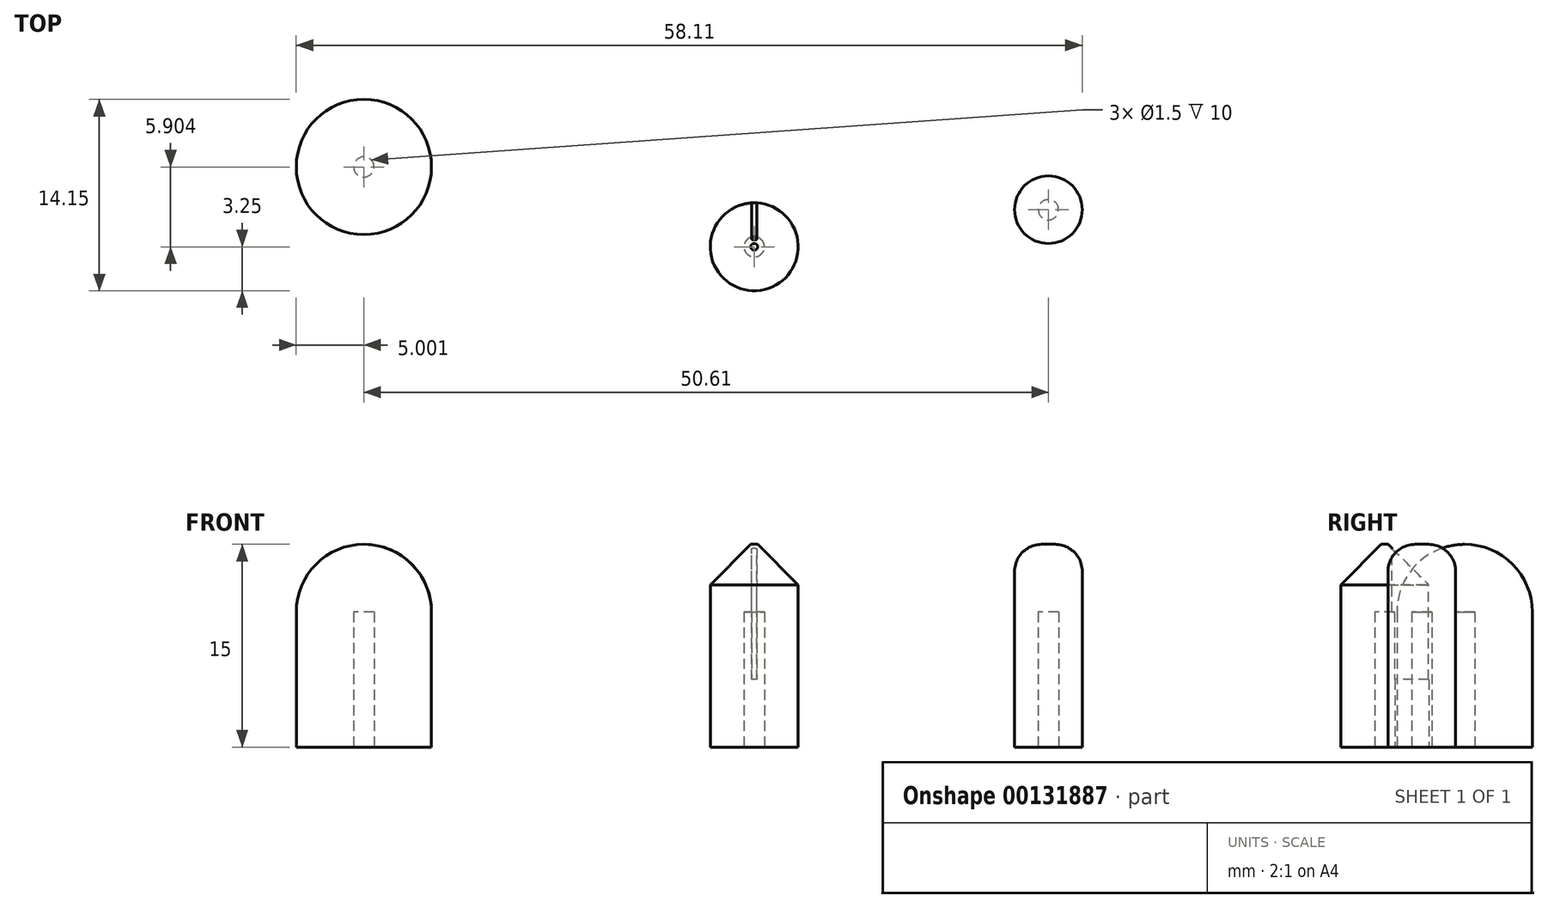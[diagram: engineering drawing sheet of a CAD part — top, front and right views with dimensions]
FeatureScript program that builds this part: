
annotation { "Feature Type Name" : "Feature", "Feature Type Description" : "" }
export const myFeature = defineFeature(function(context is Context, id is Id, definition is map)
    precondition{}
    {
        {
            var Q0;
            Q0=qCreatedBy(makeId("Top.planeOp"),FACE);
            var sketch = newSketch(context, id + "F0", { "sketchPlane" : qUnion([Q0])});
            skCircle(sketch, "E0", {"center": v(0, 0) * mm, "radius": 3.25 * mm});
            skCircle(sketch, "E1", {"center": v(21.75, 2.74) * mm, "radius": 2.5 * mm});
            skCircle(sketch, "E2", {"center": v(-28.86, 5.9) * mm, "radius": 5 * mm});
            skSolve(sketch);
        }
        {
            var Q0;
            Q0=qSketchRegion(id+"F0",true);
            extrude(context, id + "F1", {"entities" : qUnion([Q0]), "depth" : 15 * mm});
        }
        {
            var Q0;
            Q0=makeQuery(id+"F1.opExtrude","CAP_FACE",FACE,{"disambiguationData":[OSD([sQuery(id+"F0.wireOp",EDGE,"ABmODjYw-wpzC-Kf9U-QnoE-jIkIvtvc7rEM"),sQuery(id+"F0.wireOp",EDGE,"E0")])],"isStart":false});
            var sketch = newSketch(context, id + "F2", { "sketchPlane" : qUnion([Q0])});
            skLineSegment(sketch, "E3.bottom", {"start": v(0.19, 3.72) * mm, "end": v(-0.19, 3.72) * mm});
            skLineSegment(sketch, "E3.top", {"start": v(0.19, 0.52) * mm, "end": v(-0.19, 0.52) * mm});
            skLineSegment(sketch, "E3.left", {"start": v(0.19, 3.72) * mm, "end": v(0.19, 0.52) * mm});
            skLineSegment(sketch, "E3.right", {"start": v(-0.19, 3.72) * mm, "end": v(-0.19, 0.52) * mm});
            skPoint(sketch, "E3.middle", {"position": v(0, 2.12) * mm});
            skSolve(sketch);
        }
        {
            var Q0;
            {var subQ0=sQuery(id+"F2.wireOp",EDGE,"E3.left");var subQ1=makeQuery(id+"F1.opExtrude","CAP_EDGE",EDGE,{"disambiguationData":[OSD([sQuery(id+"F0.wireOp",EDGE,"E0")])],"isStart":false});var subQ2=makeQuery(id+"F2.imprint","INTERSECT",VERTEX,{"derivedFrom":[subQ1,subQ0]});Q0=makeQuery(id+"F2.imprint","IMPRINT",FACE,{"disambiguationData":[TD([[makeQuery(id+"F2.imprint","IMPRINT",EDGE,{"disambiguationData":[TD([[subQ2,-1.0]])],"derivedFrom":subQ0}),-1.0]])]});}
            extrude(context, id + "F3", {"entities" : qUnion([Q0]), "operationType" : NewBodyOperationType.REMOVE, "oppositeDirection" : true, "depth" : 10 * mm});
        }
        {
            var Q0;
            Q0=qCreatedBy(makeId("Top.planeOp"),FACE);
            var sketch = newSketch(context, id + "F4", { "sketchPlane" : qUnion([Q0])});
            skCircle(sketch, "E4", {"center": v(-28.86, 5.9) * mm, "radius": 0.75 * mm});
            skCircle(sketch, "E5", {"center": v(0, 0) * mm, "radius": 0.75 * mm});
            skCircle(sketch, "E6", {"center": v(21.75, 2.74) * mm, "radius": 0.75 * mm});
            skSolve(sketch);
        }
        {
            var Q0;
            Q0 = qSketchRegion(id + "F4", true);
            extrude(context, id + "F5", {"entities" : qUnion([Q0]), "operationType" : NewBodyOperationType.REMOVE, "depth" : 10 * mm});
        }
        {
            var Q0;
            Q0=makeQuery(id+"F1.opExtrude","CAP_EDGE",EDGE,{"disambiguationData":[OSD([sQuery(id+"F0.wireOp",EDGE,"E2")])],"isStart":false});
            fillet(context, id + "F6", {"entities" : qUnion([Q0]), "radius" : 5 * mm, "tangentPropagation" : true, "allowEdgeOverflow" : false});
        }
        {
            var Q0;
            Q0=makeQuery(id+"F1.opExtrude","CAP_EDGE",EDGE,{"disambiguationData":[OSD([sQuery(id+"F0.wireOp",EDGE,"E0")])],"isStart":false});
            chamfer(context, id + "F7", {"entities" : qUnion([Q0]), "width" : 3 * mm, "tangentPropagation" : true});
        }
        {
            var Q0;
            Q0=makeQuery(id+"F1.opExtrude","CAP_EDGE",EDGE,{"disambiguationData":[OSD([sQuery(id+"F0.wireOp",EDGE,"E1")])],"isStart":false});
            fillet(context, id + "F8", {"entities" : qUnion([Q0]), "radius" : 2 * mm, "tangentPropagation" : true, "allowEdgeOverflow" : false});
        }
    });
